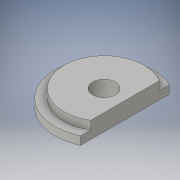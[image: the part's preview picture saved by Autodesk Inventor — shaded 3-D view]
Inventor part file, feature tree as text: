
AUTODESK INVENTOR PART (.ipt)
format: ipt  version: 2016 (Build 200138000, 138)  size: 115,712 bytes
history: native  units: in
note: dims shown in document units (in); Inventor stores cm internally (conversion verified against a paired STEP export)
features: extrude x4, sketch x4
ambient origin geometry x8: Origin, YZ Plane, XZ Plane, XY Plane, X Axis, Y Axis, Z Axis, Center Point
bodies: Solid1 (feature_tree)
feature tree (8):
  extrude  "Extrusion1"  Depth=0.08in TaperAngle=0.0deg
  extrude  "Extrusion2"  Depth=0.08in TaperAngle=0.0deg
  extrude  "Extrusion3"  Depth=0.16in TaperAngle=0.0deg
  extrude  "Extrusion4"  Depth=0.16in TaperAngle=0.0deg
  sketch  "Sketch1"  dims[d0=0.938in d1=0.08in d2=0.0in]
  sketch  "Sketch2"  dims[d3=0.768in d4=0.08in d5=0.0in]
  sketch  "Sketch3"  dims[d6=0.2165in d7=0.16in d8=0.0in]
  sketch  "Sketch4"  dims[d9=0.2in d10=0.16in d11=0.0in]
